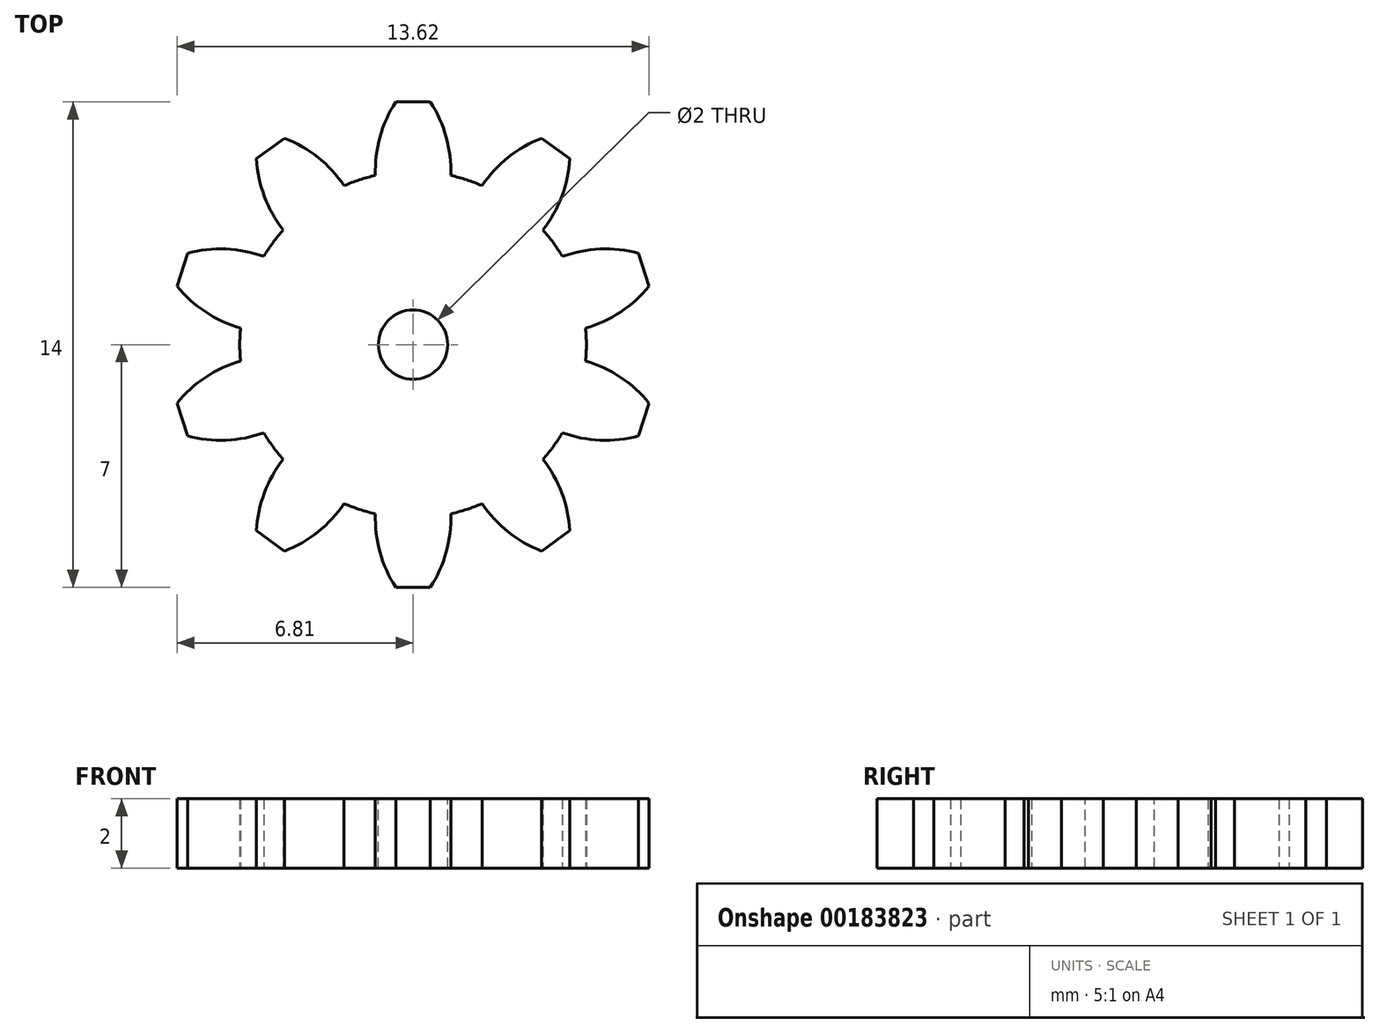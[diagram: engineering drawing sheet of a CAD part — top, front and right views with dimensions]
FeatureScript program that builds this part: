
annotation { "Feature Type Name" : "Feature", "Feature Type Description" : "" }
export const myFeature = defineFeature(function(context is Context, id is Id, definition is map)
    precondition{}
    {
        {
            var Q0;
            Q0=qCreatedBy(makeId("Top.planeOp"),FACE);
            var sketch = newSketch(context, id + "F0", { "sketchPlane" : qUnion([Q0])});
            skCircle(sketch, "E0", {"center": v(0, 0) * mm, "radius": 5 * mm});
            skLineSegment(sketch, "E1", {"start": v(0, 0) * mm, "end": v(0, 5) * mm, "construction": true});
            skLineSegment(sketch, "E2", {"start": v(0, 7) * mm, "end": v(-0.5, 7) * mm});
            skArc(sketch, "E3", {"start": v(-0.5, 7) * mm, "mid": v(-0.96, 5.98) * mm, "end": v(-1.09, 4.88) * mm});
            skLineSegment(sketch, "E4.MirrorCS", {"start": v(0, 7) * mm, "end": v(0.5, 7) * mm});
            skArc(sketch, "E5.MirrorCS", {"start": v(0.5, 7) * mm, "mid": v(0.96, 5.98) * mm, "end": v(1.09, 4.88) * mm});
            skLineSegment(sketch, "E6.1.0", {"start": v(-4.11, 5.66) * mm, "end": v(-4.52, 5.37) * mm});
            skArc(sketch, "E6.1.1", {"start": v(-4.52, 5.37) * mm, "mid": v(-4.3, 4.28) * mm, "end": v(-3.75, 3.3) * mm});
            skLineSegment(sketch, "E6.1.2", {"start": v(-4.11, 5.66) * mm, "end": v(-3.7, 5.96) * mm});
            skArc(sketch, "E6.1.3", {"start": v(-3.7, 5.96) * mm, "mid": v(-2.75, 5.4) * mm, "end": v(-1.99, 4.59) * mm});
            skLineSegment(sketch, "E6.2.0", {"start": v(-6.66, 2.16) * mm, "end": v(-6.81, 1.69) * mm});
            skArc(sketch, "E6.2.1", {"start": v(-6.81, 1.69) * mm, "mid": v(-5.99, 0.94) * mm, "end": v(-4.98, 0.47) * mm});
            skLineSegment(sketch, "E6.2.2", {"start": v(-6.66, 2.16) * mm, "end": v(-6.5, 2.64) * mm});
            skArc(sketch, "E6.2.3", {"start": v(-6.5, 2.64) * mm, "mid": v(-5.4, 2.76) * mm, "end": v(-4.3, 2.54) * mm});
            skLineSegment(sketch, "E6.3.0", {"start": v(-6.66, -2.16) * mm, "end": v(-6.5, -2.64) * mm});
            skArc(sketch, "E6.3.1", {"start": v(-6.5, -2.64) * mm, "mid": v(-5.4, -2.76) * mm, "end": v(-4.3, -2.54) * mm});
            skLineSegment(sketch, "E6.3.2", {"start": v(-6.66, -2.16) * mm, "end": v(-6.81, -1.69) * mm});
            skArc(sketch, "E6.3.3", {"start": v(-6.81, -1.69) * mm, "mid": v(-5.99, -0.94) * mm, "end": v(-4.98, -0.47) * mm});
            skLineSegment(sketch, "E6.4.0", {"start": v(-4.11, -5.66) * mm, "end": v(-3.7, -5.96) * mm});
            skArc(sketch, "E6.4.1", {"start": v(-3.7, -5.96) * mm, "mid": v(-2.75, -5.4) * mm, "end": v(-1.99, -4.59) * mm});
            skLineSegment(sketch, "E6.4.2", {"start": v(-4.11, -5.66) * mm, "end": v(-4.52, -5.37) * mm});
            skArc(sketch, "E6.4.3", {"start": v(-4.52, -5.37) * mm, "mid": v(-4.3, -4.28) * mm, "end": v(-3.75, -3.3) * mm});
            skLineSegment(sketch, "E6.5.0", {"start": v(0, -7) * mm, "end": v(0.5, -7) * mm});
            skArc(sketch, "E6.5.1", {"start": v(0.5, -7) * mm, "mid": v(0.96, -5.98) * mm, "end": v(1.09, -4.88) * mm});
            skLineSegment(sketch, "E6.5.2", {"start": v(0, -7) * mm, "end": v(-0.5, -7) * mm});
            skArc(sketch, "E6.5.3", {"start": v(-0.5, -7) * mm, "mid": v(-0.96, -5.98) * mm, "end": v(-1.09, -4.88) * mm});
            skLineSegment(sketch, "E6.6.0", {"start": v(4.11, -5.66) * mm, "end": v(4.52, -5.37) * mm});
            skArc(sketch, "E6.6.1", {"start": v(4.52, -5.37) * mm, "mid": v(4.3, -4.28) * mm, "end": v(3.75, -3.3) * mm});
            skLineSegment(sketch, "E6.6.2", {"start": v(4.11, -5.66) * mm, "end": v(3.7, -5.96) * mm});
            skArc(sketch, "E6.6.3", {"start": v(3.7, -5.96) * mm, "mid": v(2.75, -5.4) * mm, "end": v(1.99, -4.59) * mm});
            skLineSegment(sketch, "E6.7.0", {"start": v(6.66, -2.16) * mm, "end": v(6.81, -1.69) * mm});
            skArc(sketch, "E6.7.1", {"start": v(6.81, -1.69) * mm, "mid": v(5.99, -0.94) * mm, "end": v(4.98, -0.47) * mm});
            skLineSegment(sketch, "E6.7.2", {"start": v(6.66, -2.16) * mm, "end": v(6.5, -2.64) * mm});
            skArc(sketch, "E6.7.3", {"start": v(6.5, -2.64) * mm, "mid": v(5.4, -2.76) * mm, "end": v(4.3, -2.54) * mm});
            skLineSegment(sketch, "E6.8.0", {"start": v(6.66, 2.16) * mm, "end": v(6.5, 2.64) * mm});
            skArc(sketch, "E6.8.1", {"start": v(6.5, 2.64) * mm, "mid": v(5.4, 2.76) * mm, "end": v(4.3, 2.54) * mm});
            skLineSegment(sketch, "E6.8.2", {"start": v(6.66, 2.16) * mm, "end": v(6.81, 1.69) * mm});
            skArc(sketch, "E6.8.3", {"start": v(6.81, 1.69) * mm, "mid": v(5.99, 0.94) * mm, "end": v(4.98, 0.47) * mm});
            skLineSegment(sketch, "E6.9.0", {"start": v(4.11, 5.66) * mm, "end": v(3.7, 5.96) * mm});
            skArc(sketch, "E6.9.1", {"start": v(3.7, 5.96) * mm, "mid": v(2.75, 5.4) * mm, "end": v(1.99, 4.59) * mm});
            skLineSegment(sketch, "E6.9.2", {"start": v(4.11, 5.66) * mm, "end": v(4.52, 5.37) * mm});
            skArc(sketch, "E6.9.3", {"start": v(4.52, 5.37) * mm, "mid": v(4.3, 4.28) * mm, "end": v(3.75, 3.3) * mm});
            skSolve(sketch);
        }
        {
            var Q0;
            Q0=qSketchRegion(id+"F0",true);
            extrude(context, id + "F1", {"entities" : qUnion([Q0]), "depth" : 2 * mm});
        }
        {
            var Q0;
            Q0=makeQuery(id+"F1.opExtrude","CAP_FACE",FACE,{"disambiguationData":[OSD([sQuery(id+"F0.wireOp",EDGE,"E0"),sQuery(id+"F0.wireOp",EDGE,"E2"),sQuery(id+"F0.wireOp",EDGE,"E3"),sQuery(id+"F0.wireOp",EDGE,"E4.MirrorCS"),sQuery(id+"F0.wireOp",EDGE,"E5.MirrorCS"),sQuery(id+"F0.wireOp",EDGE,"E6.1.0"),sQuery(id+"F0.wireOp",EDGE,"E6.1.1"),sQuery(id+"F0.wireOp",EDGE,"E6.1.2"),sQuery(id+"F0.wireOp",EDGE,"E6.1.3"),sQuery(id+"F0.wireOp",EDGE,"E6.2.0"),sQuery(id+"F0.wireOp",EDGE,"E6.2.1"),sQuery(id+"F0.wireOp",EDGE,"E6.2.2"),sQuery(id+"F0.wireOp",EDGE,"E6.2.3"),sQuery(id+"F0.wireOp",EDGE,"E6.3.0"),sQuery(id+"F0.wireOp",EDGE,"E6.3.1"),sQuery(id+"F0.wireOp",EDGE,"E6.3.2"),sQuery(id+"F0.wireOp",EDGE,"E6.3.3"),sQuery(id+"F0.wireOp",EDGE,"E6.4.0"),sQuery(id+"F0.wireOp",EDGE,"E6.4.1"),sQuery(id+"F0.wireOp",EDGE,"E6.4.2"),sQuery(id+"F0.wireOp",EDGE,"E6.4.3"),sQuery(id+"F0.wireOp",EDGE,"E6.5.0"),sQuery(id+"F0.wireOp",EDGE,"E6.5.1"),sQuery(id+"F0.wireOp",EDGE,"E6.5.2"),sQuery(id+"F0.wireOp",EDGE,"E6.5.3"),sQuery(id+"F0.wireOp",EDGE,"E6.6.0"),sQuery(id+"F0.wireOp",EDGE,"E6.6.1"),sQuery(id+"F0.wireOp",EDGE,"E6.6.2"),sQuery(id+"F0.wireOp",EDGE,"E6.6.3"),sQuery(id+"F0.wireOp",EDGE,"E6.7.0"),sQuery(id+"F0.wireOp",EDGE,"E6.7.1"),sQuery(id+"F0.wireOp",EDGE,"E6.7.2"),sQuery(id+"F0.wireOp",EDGE,"E6.7.3"),sQuery(id+"F0.wireOp",EDGE,"E6.8.0"),sQuery(id+"F0.wireOp",EDGE,"E6.8.1"),sQuery(id+"F0.wireOp",EDGE,"E6.8.2"),sQuery(id+"F0.wireOp",EDGE,"E6.8.3"),sQuery(id+"F0.wireOp",EDGE,"E6.9.0"),sQuery(id+"F0.wireOp",EDGE,"E6.9.1"),sQuery(id+"F0.wireOp",EDGE,"E6.9.2"),sQuery(id+"F0.wireOp",EDGE,"E6.9.3"),sQuery(id+"F0.wireOp",EDGE,"E6.10.0"),sQuery(id+"F0.wireOp",EDGE,"E6.10.1"),sQuery(id+"F0.wireOp",EDGE,"E6.10.2"),sQuery(id+"F0.wireOp",EDGE,"E6.10.3"),sQuery(id+"F0.wireOp",EDGE,"E6.11.0"),sQuery(id+"F0.wireOp",EDGE,"E6.11.1"),sQuery(id+"F0.wireOp",EDGE,"E6.11.2"),sQuery(id+"F0.wireOp",EDGE,"E6.11.3"),sQuery(id+"F0.wireOp",EDGE,"E6.12.0"),sQuery(id+"F0.wireOp",EDGE,"E6.12.1"),sQuery(id+"F0.wireOp",EDGE,"E6.12.2"),sQuery(id+"F0.wireOp",EDGE,"E6.12.3"),sQuery(id+"F0.wireOp",EDGE,"E6.13.0"),sQuery(id+"F0.wireOp",EDGE,"E6.13.1"),sQuery(id+"F0.wireOp",EDGE,"E6.13.2"),sQuery(id+"F0.wireOp",EDGE,"E6.13.3"),sQuery(id+"F0.wireOp",EDGE,"E6.14.0"),sQuery(id+"F0.wireOp",EDGE,"E6.14.1"),sQuery(id+"F0.wireOp",EDGE,"E6.14.2"),sQuery(id+"F0.wireOp",EDGE,"E6.14.3"),sQuery(id+"F0.wireOp",EDGE,"E6.15.0"),sQuery(id+"F0.wireOp",EDGE,"E6.15.1"),sQuery(id+"F0.wireOp",EDGE,"E6.15.2"),sQuery(id+"F0.wireOp",EDGE,"E6.15.3")])],"isStart":false});
            var sketch = newSketch(context, id + "F2", { "sketchPlane" : qUnion([Q0])});
            skCircle(sketch, "E7", {"center": v(0, 0) * mm, "radius": 1 * mm});
            skSolve(sketch);
        }
        {
            var Q0;
            Q0=qSketchRegion(id+"F2",true);
            extrude(context, id + "F3", {"entities" : qUnion([Q0]), "operationType" : NewBodyOperationType.REMOVE, "endBound" : BoundingType.THROUGH_ALL, "oppositeDirection" : true, "depth" : 25 * mm});
        }
    });
